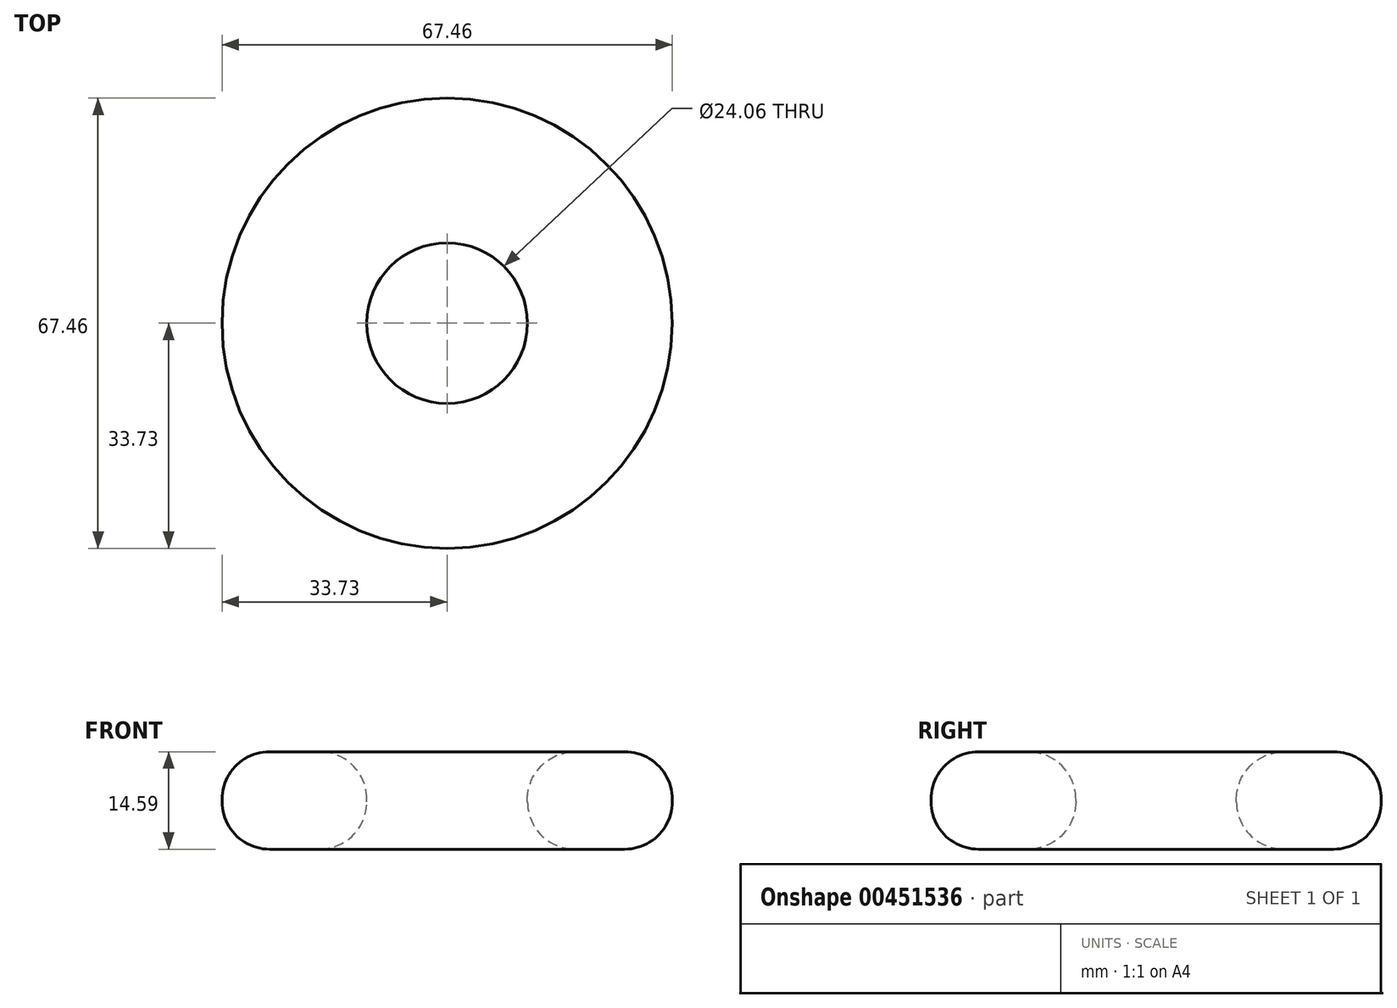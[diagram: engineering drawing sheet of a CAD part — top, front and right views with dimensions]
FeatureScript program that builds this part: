
annotation { "Feature Type Name" : "Feature", "Feature Type Description" : "" }
export const myFeature = defineFeature(function(context is Context, id is Id, definition is map)
    precondition{}
    {
        {
            var Q0;
            Q0=qCreatedBy(makeId("Front.planeOp"),FACE);
            var sketch = newSketch(context, id + "F0", { "sketchPlane" : qUnion([Q0])});
            skLineSegment(sketch, "E0", {"start": v(0, 68.77) * mm, "end": v(0, -99.38) * mm, "construction": true});
            skLineSegment(sketch, "E1.bottom", {"start": v(-33.73, 30.76) * mm, "end": v(-12.03, 30.76) * mm});
            skLineSegment(sketch, "E1.top", {"start": v(-33.73, 16.17) * mm, "end": v(-12.03, 16.17) * mm});
            skLineSegment(sketch, "E1.left", {"start": v(-33.73, 30.76) * mm, "end": v(-33.73, 16.17) * mm});
            skLineSegment(sketch, "E1.right", {"start": v(-12.03, 30.76) * mm, "end": v(-12.03, 16.17) * mm});
            skSolve(sketch);
        }
        {
            var Q0;
            Q0=makeQuery(id+"F0.imprint","IMPRINT",FACE,{"disambiguationData":[TD([[makeQuery(id+"F0.imprint","IMPRINT",EDGE,{"derivedFrom":sQuery(id+"F0.wireOp",EDGE,"E1.bottom")}),-1.0]])]});
            var Q1;
            Q1=sQuery(id+"F0.wireOp",EDGE,"E0");
            revolve(context, id + "F1", {"entities" : qUnion([Q0]), "axis" : qUnion([Q1]), "revolveType" : RevolveType.FULL});
        }
        {
            var Q0;
            Q0=makeQuery(id+"F1.opRevolve","SWEPT_FACE",FACE,{"disambiguationData":[OSD([sQuery(id+"F0.wireOp",EDGE,"E1.left")])]});
            var Q1;
            Q1=makeQuery(id+"F1.opRevolve","SWEPT_FACE",FACE,{"disambiguationData":[OSD([sQuery(id+"F0.wireOp",EDGE,"E1.right")])]});
            fillet(context, id + "F2", {"entities" : qUnion([Q0, Q1]), "radius" : 7.11 * mm, "tangentPropagation" : true, "allowEdgeOverflow" : false});
        }
    });
